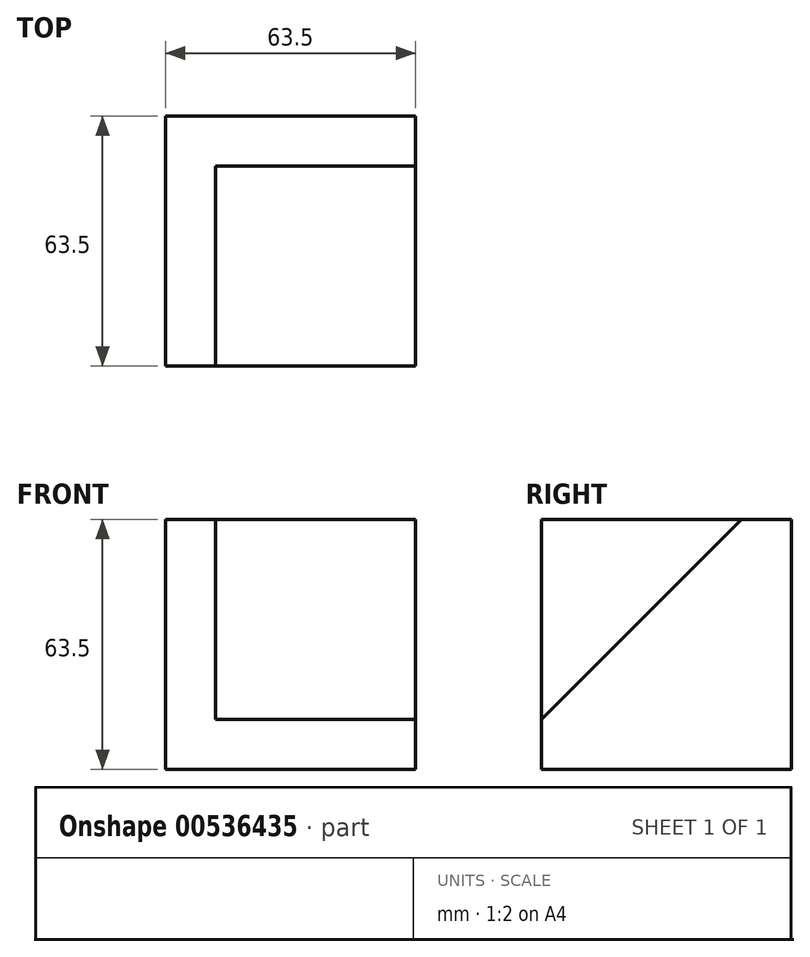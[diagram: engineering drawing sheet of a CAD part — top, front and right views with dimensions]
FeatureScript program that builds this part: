
annotation { "Feature Type Name" : "Feature", "Feature Type Description" : "" }
export const myFeature = defineFeature(function(context is Context, id is Id, definition is map)
    precondition{}
    {
        {
            var Q0;
            Q0=qCreatedBy(makeId("Front.planeOp"),FACE);
            var sketch = newSketch(context, id + "F0", { "sketchPlane" : qUnion([Q0])});
            skLineSegment(sketch, "E0", {"start": v(0, 0) * mm, "end": v(63.5, 0) * mm});
            skLineSegment(sketch, "E1", {"start": v(63.5, 0) * mm, "end": v(63.5, 63.5) * mm});
            skLineSegment(sketch, "E2", {"start": v(63.5, 63.5) * mm, "end": v(0, 63.5) * mm});
            skLineSegment(sketch, "E3", {"start": v(0, 63.5) * mm, "end": v(0, 0) * mm});
            skSolve(sketch);
        }
        {
            var Q0;
            Q0=makeQuery(id+"F0.imprint","IMPRINT",FACE,{"disambiguationData":[TD([[makeQuery(id+"F0.imprint","IMPRINT",EDGE,{"derivedFrom":sQuery(id+"F0.wireOp",EDGE,"E0")}),1.0]])]});
            extrude(context, id + "F1", {"entities" : qUnion([Q0]), "depth" : 63.5 * mm, "offsetDistance" : 25.4 * mm});
        }
        {
            var Q0;
            Q0=makeQuery(id+"F1.opExtrude","SWEPT_FACE",FACE,{"disambiguationData":[OSD([sQuery(id+"F0.wireOp",EDGE,"E1")])]});
            var sketch = newSketch(context, id + "F2", { "sketchPlane" : qUnion([Q0])});
            skLineSegment(sketch, "E4", {"start": v(-12.7, 63.5) * mm, "end": v(-63.5, 12.7) * mm});
            skSolve(sketch);
        }
        {
            var Q0;
            Q0=makeQuery(id+"F1.opExtrude","CAP_FACE",FACE,{"disambiguationData":[OSD([sQuery(id+"F0.wireOp",EDGE,"E0"),sQuery(id+"F0.wireOp",EDGE,"E1"),sQuery(id+"F0.wireOp",EDGE,"E2"),sQuery(id+"F0.wireOp",EDGE,"E3")])],"isStart":false});
            var sketch = newSketch(context, id + "F3", { "sketchPlane" : qUnion([Q0])});
            skLineSegment(sketch, "E5", {"start": v(12.7, 63.5) * mm, "end": v(12.7, 0) * mm});
            skLineSegment(sketch, "E6", {"start": v(12.7, 0) * mm, "end": v(13.94, 1.08) * mm});
            skSolve(sketch);
        }
        {
            var Q0;
            {var subQ0=sQuery(id+"F2.wireOp",EDGE,"E4");Q0=makeQuery(id+"F2.imprint","IMPRINT",FACE,{"disambiguationData":[TD([[makeQuery(id+"F2.imprint","IMPRINT",EDGE,{"derivedFrom":subQ0}),-1.0]])]});}
            extrude(context, id + "F4", {"entities" : qUnion([Q0]), "operationType" : NewBodyOperationType.REMOVE, "oppositeDirection" : true, "depth" : 50.8 * mm, "offsetDistance" : 25.4 * mm});
        }
    });
